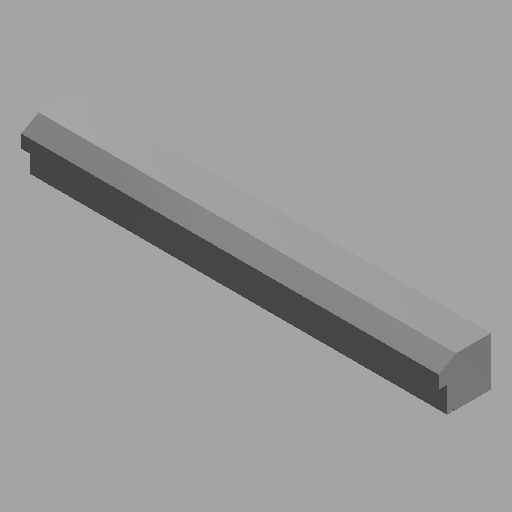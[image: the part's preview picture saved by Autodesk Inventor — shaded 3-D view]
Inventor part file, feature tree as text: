
AUTODESK INVENTOR PART (.ipt)
format: ipt  version: 2023 (Build 270158030, 158C)  size: 103,936 bytes
history: native  units: mm (DEFAULTED — no unit token found)
features: extrude x2, sketch x2
ambient origin geometry x8: Origin, YZ Plane, XZ Plane, XY Plane, X Axis, Y Axis, Z Axis, Center Point
bodies: Solid1 (feature_tree)
feature tree (4):
  extrude  "Extrusion1"  Depth=25.4mm TaperAngle=0.0deg
  extrude  "Extrusion2"  [1 undecoded]
  sketch  "Sketch1"  dims[d0=25.4mm d1=0.0mm d2=25.4mm d3=0.0mm]
  sketch  "Sketch2"
note: 1 required parameter value undecoded (feature->parameter linkage not recoverable at this tier; creation-order binding heuristic only, values carry confidence <= 0.55)
